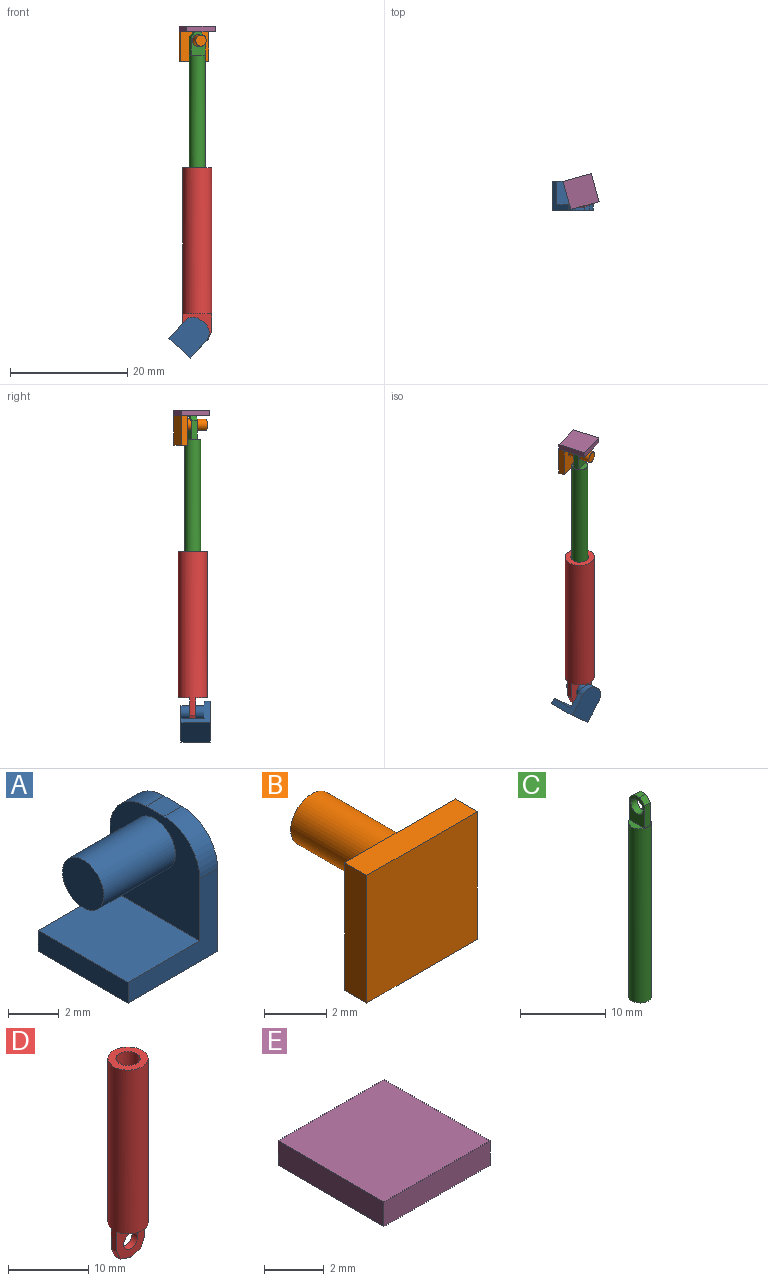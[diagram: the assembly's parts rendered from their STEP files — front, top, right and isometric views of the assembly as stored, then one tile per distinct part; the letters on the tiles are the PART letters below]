
ASSEMBLY  parts=5 mates=4
PART A: 12 faces, bbox 5x5x6 mm
  f0: plane 5x4mm, normal (0,0,1), area 20mm2, adj f1,f3,f4,f7
  f1: plane 5x4mm, normal (0,-1,0), area 8mm2, adj f0,f2,f4,f5,f7,f11
  f2: plane 6x5mm, normal (1,0,0), area 28.3mm2, adj f1,f3,f5,f6,f10,f11
  f3: plane 5x4mm, normal (0,1,0), area 8mm2, adj f0,f2,f4,f5,f7,f10
  f4: plane 5x1mm, normal (-1,0,0), area 5mm2, adj f0,f1,f3,f5
  f5: plane 5x5mm, normal (0,0,-1), area 25mm2, adj f1,f2,f3,f4
  f6: plane 1x1mm, normal (0,0,1), area 1mm2, adj f2,f7,f10,f11
  f7: plane 5x5mm, normal (-1,0,0), area 19.1mm2, adj f0,f1,f3,f6,f8,f10,f11
  f8: cylinder r=1.15mm len=4mm, axis (1,0,0), area 28.9mm2, adj f7,f9
  f9: plane 2.3x2.3mm, normal (-1,0,0), area 4.2mm2, adj f8
  f10: cylinder r=2mm len=2mm, axis (1,0,0), area 3.1mm2, adj f2,f3,f6,f7
  f11: cylinder r=2mm len=2mm, axis (-1,0,0), area 3.1mm2, adj f1,f2,f6,f7
PART B: 8 faces, bbox 5x5x5 mm
  f0: plane 5x1mm, normal (-1,0,0), area 5mm2, adj f1,f3,f4,f5
  f1: plane 5x1mm, normal (0,0,-1), area 5mm2, adj f0,f2,f4,f5
  f2: plane 5x1mm, normal (1,0,0), area 5mm2, adj f1,f3,f4,f5
  f3: plane 5x1mm, normal (0,0,1), area 5mm2, adj f0,f2,f4,f5
  f4: plane 5x5mm, normal (0,1,0), area 22.2mm2, adj f0,f1,f2,f3,f6
  f5: plane 5x5mm, normal (0,-1,0), area 25mm2, adj f0,f1,f2,f3
  f6: cylinder r=0.95mm len=4mm, axis (0,-1,0), area 23.9mm2, adj f4,f7
  f7: plane 1.9x1.9mm, normal (0,1,0), area 2.8mm2, adj f6
PART C: 14 faces, bbox 2.7x2.7x29 mm
  f0: plane 2.51x0.85mm, normal (0,0,1), area 1.5mm2, adj f3,f6
  f1: plane 1x0.1mm, normal (0,0,1), area 0.1mm2, adj f3,f9
  f2: plane 2.51x0.85mm, normal (0,0,1), area 1.5mm2, adj f3,f8
  f3: cylinder r=1.35mm len=25mm, axis (0,0,-1), area 212.1mm2, adj f0,f1,f2,f4,f5
  f4: plane 1x0.1mm, normal (0,0,1), area 0.1mm2, adj f3,f7
  f5: plane 2.7x2.7mm, normal (0,0,-1), area 5.7mm2, adj f3
  f6: plane 4.02x2.51mm, normal (-1,0,0), area 6.3mm2, adj f0,f7,f9,f10,f11,f12,f13
  f7: plane 3.23x1mm, normal (0,-1,0), area 3.2mm2, adj f4,f6,f8,f12
  f8: plane 4.02x2.51mm, normal (1,0,0), area 6.3mm2, adj f2,f7,f9,f10,f11,f12,f13
  f9: plane 3.23x1mm, normal (0,1,0), area 3.2mm2, adj f1,f6,f8,f13
  f10: cylinder r=1mm len=2mm, axis (-1,0,0), area 6.3mm2, adj f6,f8
  f11: plane 1x0.93mm, normal (0,0,1), area 0.9mm2, adj f6,f8,f12,f13
  f12: plane 1x0.79mm, normal (0,-0.71,0.71), area 1.1mm2, adj f6,f7,f8,f11
  f13: plane 1x0.79mm, normal (0,0.71,0.71), area 1.1mm2, adj f6,f8,f9,f11
PART D: 14 faces, bbox 5x5x30 mm
  f0: plane 4.9x2mm, normal (0,0,-1), area 7.3mm2, adj f1,f7
  f1: cylinder r=2.5mm len=28mm, axis (0,0,-1), area 398.7mm2, adj f0,f2,f4,f6,f7,f10,f12
  f2: plane 4.9x2mm, normal (0,0,-1), area 7.3mm2, adj f1,f6
  f3: cylinder r=1.5mm len=23mm, axis (0,0,-1), area 216.8mm2, adj f4,f5
  f4: plane 5x5mm, normal (0,0,1), area 12.6mm2, adj f1,f3
  f5: plane 3x3mm, normal (0,0,1), area 7.1mm2, adj f3
  f6: plane 5.02x4.92mm, normal (0,1,0), area 17.1mm2, adj f1,f2,f9,f10,f11,f12,f13
  f7: plane 5.02x4.92mm, normal (0,-1,0), area 17.1mm2, adj f0,f1,f9,f10,f11,f12,f13
  f8: plane 1x1mm, normal (0,0,-1), area 0.8mm2, adj f11,f13
  f9: cylinder r=1.25mm len=2.5mm, axis (0,1,0), area 7.9mm2, adj f6,f7
  f10: cone r=2.5mm half-angle=22.5deg, axis (0,0,1), area 1.6mm2, adj f1,f6,f7,f11
  f11: cone r=0.5mm half-angle=67.5deg, axis (0,0,1), area 1.6mm2, adj f6,f7,f8,f10
  f12: cone r=2.5mm half-angle=22.5deg, axis (0,0,1), area 1.6mm2, adj f1,f6,f7,f13
  f13: cone r=0.5mm half-angle=67.5deg, axis (0,0,1), area 1.6mm2, adj f6,f7,f8,f12
PART E: 6 faces, bbox 5x5x1 mm
  f0: plane 5x1mm, normal (0,-1,0), area 5mm2, adj f1,f3,f4,f5
  f1: plane 5x1mm, normal (1,0,0), area 5mm2, adj f0,f2,f4,f5
  f2: plane 5x1mm, normal (0,1,0), area 5mm2, adj f1,f3,f4,f5
  f3: plane 5x1mm, normal (-1,0,0), area 5mm2, adj f0,f2,f4,f5
  f4: plane 5x5mm, normal (0,0,1), area 25mm2, adj f0,f1,f2,f3
  f5: plane 5x5mm, normal (0,0,-1), area 25mm2, adj f0,f1,f2,f3
PLACE A rot(axis=(-0.33,0.33,-0.88),97.1deg) t=(-23.54,5.43,-8.16)mm
PLACE B rot(axis=(0,0,-1),164.3deg) t=(-20.61,6.08,40.92)mm
PLACE C rot(axis=(0,0,1),105.7deg) t=(-20.57,5.93,16.92)mm
PLACE D t=(-20.57,5.93,-2.27)mm fixed
PLACE E rot(axis=(-0.8,0.6,0),180deg) t=(-20.61,6.08,46.92)mm
MATE slider C.f10 <-> B.f6  axis (0.27,-0.96,0) through (-20.57,5.93,44.42)mm
MATE fastened B.f3 <-> E.f4  axis (0,0,1) through (-21.29,8.49,45.92)mm
MATE revolute D.f9 <-> A.f8  axis (0,1,0) through (-20.57,5.93,-4.77)mm
MATE cylindrical C.f3 <-> D.f1  axis (0,0,-1) through (-20.57,5.93,29.42)mm
